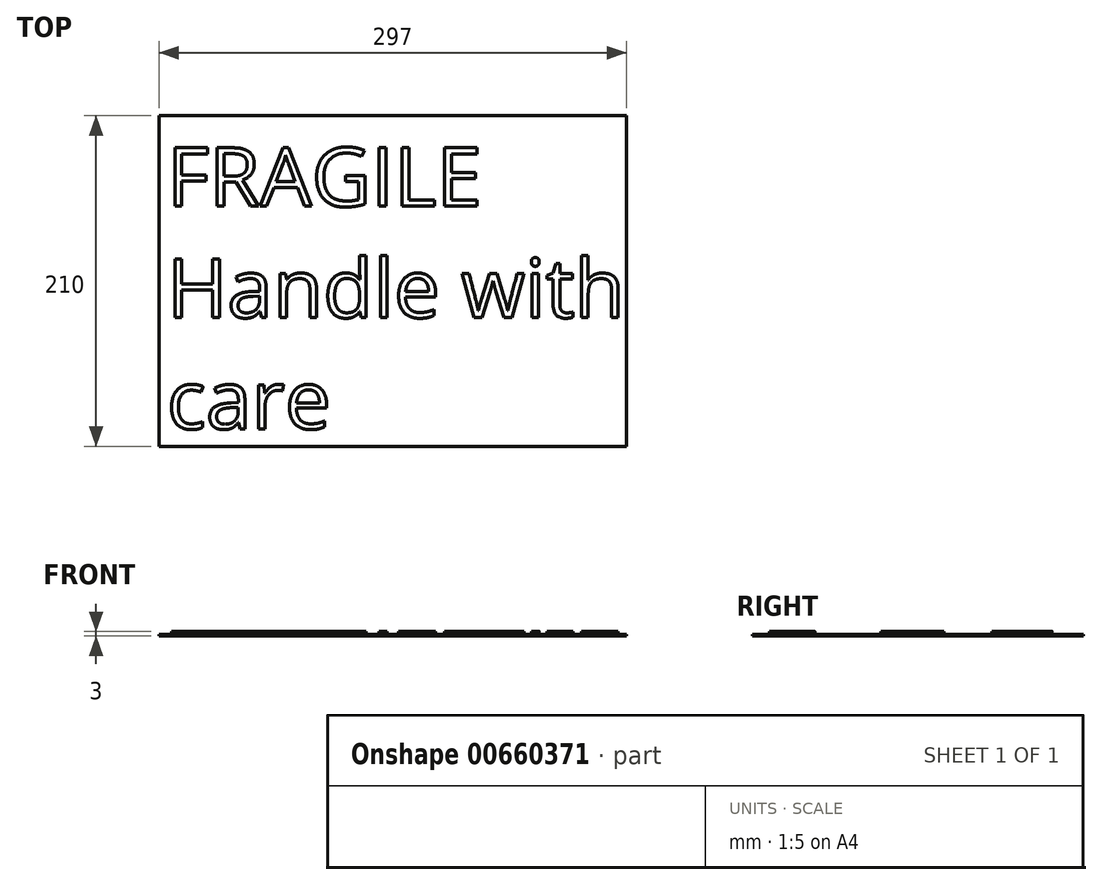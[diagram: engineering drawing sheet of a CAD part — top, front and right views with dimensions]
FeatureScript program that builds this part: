
annotation { "Feature Type Name" : "Feature", "Feature Type Description" : "" }
export const myFeature = defineFeature(function(context is Context, id is Id, definition is map)
    precondition{}
    {
        {
            var Q0;
            Q0=qCreatedBy(makeId("Top.planeOp"),FACE);
            var sketch = newSketch(context, id + "F0", { "sketchPlane" : qUnion([Q0])});
            skLineSegment(sketch, "E0.bottom", {"start": v(-226.49, 160.02) * mm, "end": v(70.51, 160.02) * mm});
            skLineSegment(sketch, "E0.top", {"start": v(-226.49, -49.98) * mm, "end": v(70.51, -49.98) * mm});
            skLineSegment(sketch, "E0.left", {"start": v(-226.49, 160.02) * mm, "end": v(-226.49, -49.98) * mm});
            skLineSegment(sketch, "E0.right", {"start": v(70.51, 160.02) * mm, "end": v(70.51, -49.98) * mm});
            skSolve(sketch);
        }
        {
            var Q0;
            Q0=qSketchRegion(id+"F0",true);
            extrude(context, id + "F1", {"entities" : qUnion([Q0]), "depth" : 1 * mm, "offsetDistance" : 25 * mm});
        }
        {
            var Q0;
            Q0=makeQuery(id+"F1.opExtrude","CAP_FACE",FACE,{"disambiguationData":[OSD([sQuery(id+"F0.wireOp",EDGE,"E0.bottom"),sQuery(id+"F0.wireOp",EDGE,"E0.top"),sQuery(id+"F0.wireOp",EDGE,"E0.left"),sQuery(id+"F0.wireOp",EDGE,"E0.right")])],"isStart":false});
            var sketch = newSketch(context, id + "F2", { "sketchPlane" : qUnion([Q0])});
            skText(sketch, "E1", { "text": "FRAGILE\nHandle with\ncare", "fontName": "OpenSans-Regular.ttf"});
            const initialGuessF2  = {"E1": [-0.22149, 0.10257, 1, 0, 0.03744]};
            skSetInitialGuess(sketch, initialGuessF2);
            skSolve(sketch);
        }
        {
            var Q0;
            Q0=qSketchRegion(id+"F2",true);
            extrude(context, id + "F3", {"entities" : qUnion([Q0]), "operationType" : NewBodyOperationType.ADD, "depth" : 2 * mm, "offsetDistance" : 25 * mm});
        }
    });
